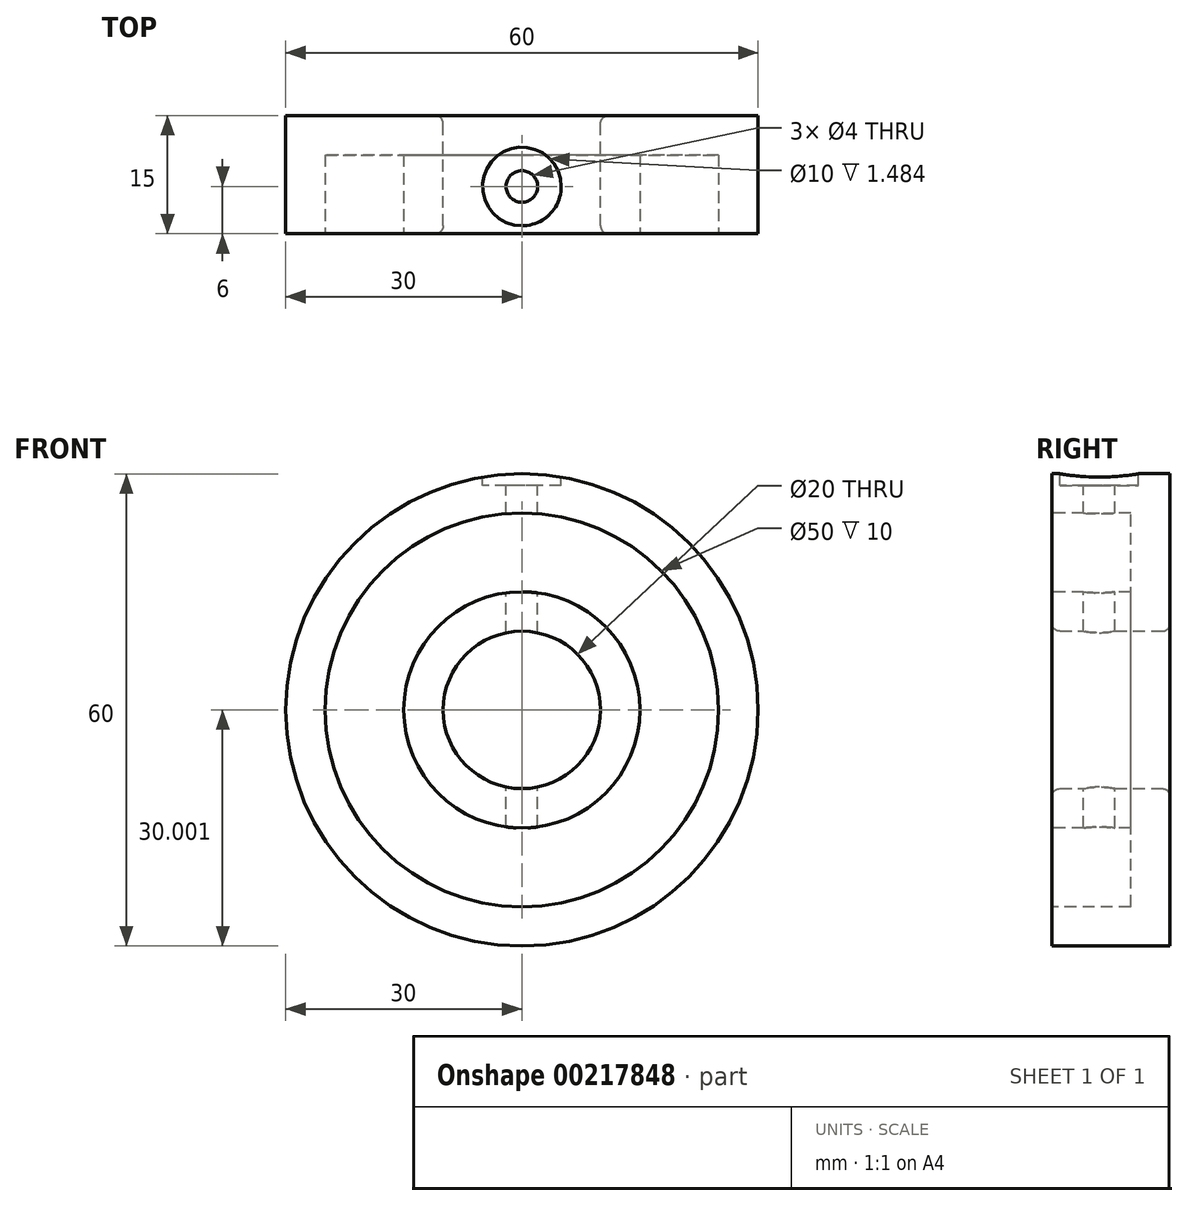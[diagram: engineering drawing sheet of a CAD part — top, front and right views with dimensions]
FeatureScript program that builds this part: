
annotation { "Feature Type Name" : "Feature", "Feature Type Description" : "" }
export const myFeature = defineFeature(function(context is Context, id is Id, definition is map)
    precondition{}
    {
        {
            var Q0;
            Q0=qCreatedBy(makeId("Front.planeOp"),FACE);
            var sketch = newSketch(context, id + "F0", { "sketchPlane" : qUnion([Q0])});
            skCircle(sketch, "E0", {"center": v(0, -30.02) * mm, "radius": 30 * mm});
            skCircle(sketch, "E1", {"center": v(0, -30.02) * mm, "radius": 10 * mm});
            skSolve(sketch);
        }
        {
            var Q0;
            Q0=makeQuery(id+"F0.imprint","IMPRINT",FACE,{"disambiguationData":[TD([[makeQuery(id+"F0.imprint","IMPRINT",EDGE,{"derivedFrom":sQuery(id+"F0.wireOp",EDGE,"E0")}),1.0]])]});
            extrude(context, id + "F1", {"entities" : qUnion([Q0]), "depth" : 15 * mm});
        }
        {
            var Q0;
            Q0=qCreatedBy(makeId("Top.planeOp"),FACE);
            var sketch = newSketch(context, id + "F2", { "sketchPlane" : qUnion([Q0])});
            skCircle(sketch, "E2", {"center": v(0, -9) * mm, "radius": 5 * mm});
            skSolve(sketch);
        }
        {
            var Q0;
            Q0 = qSketchRegion(id + "F2", true);
            extrude(context, id + "F3", {"entities" : qUnion([Q0]), "operationType" : NewBodyOperationType.REMOVE, "oppositeDirection" : true, "depth" : 1.5 * mm});
        }
        {
            var Q0;
            Q0=makeQuery(id+"F1.opExtrude","CAP_FACE",FACE,{"disambiguationData":[OSD([sQuery(id+"F0.wireOp",EDGE,"E0"),sQuery(id+"F0.wireOp",EDGE,"E1")])],"isStart":false});
            var sketch = newSketch(context, id + "F4", { "sketchPlane" : qUnion([Q0])});
            skCircle(sketch, "E3", {"center": v(0, -30.02) * mm, "radius": 15 * mm});
            skCircle(sketch, "E4", {"center": v(0, -30.02) * mm, "radius": 25 * mm});
            skSolve(sketch);
        }
        {
            var Q0;
            Q0=makeQuery(id+"F4.imprint","IMPRINT",FACE,{"disambiguationData":[TD([[makeQuery(id+"F4.imprint","IMPRINT",EDGE,{"derivedFrom":sQuery(id+"F4.wireOp",EDGE,"E3")}),-1.0]])]});
            extrude(context, id + "F5", {"entities" : qUnion([Q0]), "operationType" : NewBodyOperationType.REMOVE, "oppositeDirection" : true, "depth" : 10 * mm});
        }
        {
            var Q0;
            Q0=qCreatedBy(makeId("Top.planeOp"),FACE);
            var sketch = newSketch(context, id + "F6", { "sketchPlane" : qUnion([Q0])});
            skCircle(sketch, "E5", {"center": v(0, -9) * mm, "radius": 2.5 * mm});
            skSolve(sketch);
        }
        {
            var Q0;
            Q0=sQuery(id+"F6.wireOp",VERTEX,"E5.center");
            var Q1;
            Q1=makeQuery(id+"F1.opExtrude","SWEPT_BODY",BODY,{"disambiguationData":[OSD([sQuery(id+"F0.wireOp",EDGE,"E0"),sQuery(id+"F0.wireOp",EDGE,"E1")])]});
            hole(context, id + "F7", {"style" : HoleStyle.SIMPLE, "endStyle" : HoleEndStyle.BLIND, "standardTappedOrClearance" : lookupTablePath({ "standard" : "ISO", "engagement" : "75%", "pitch" : "1 mm", "size" : "M5", "type" : "Tapped" }), "standardBlindInLast" : lookupTablePath({ "standard" : "ISO", "engagement" : "75%", "pitch" : "1 mm", "size" : "M5", "type" : "Tapped" }), "holeDiameter" : 4 * mm, "holeDepth" : 45 * mm, "startFromSketch" : true, "locations" : qUnion([Q0]), "scope" : qUnion([Q1])});
        }
        {
            var Q0;
            Q0=makeQuery(id+"F1.opExtrude","CAP_EDGE",EDGE,{"disambiguationData":[OSD([sQuery(id+"F0.wireOp",EDGE,"E1")])],"isStart":true});
            var Q1;
            Q1=makeQuery(id+"F1.opExtrude","CAP_EDGE",EDGE,{"disambiguationData":[OSD([sQuery(id+"F0.wireOp",EDGE,"E1")])],"isStart":false});
            fillet(context, id + "F8", {"entities" : qUnion([Q0, Q1]), "radius" : 1 * mm, "tangentPropagation" : true, "allowEdgeOverflow" : false});
        }
    });
